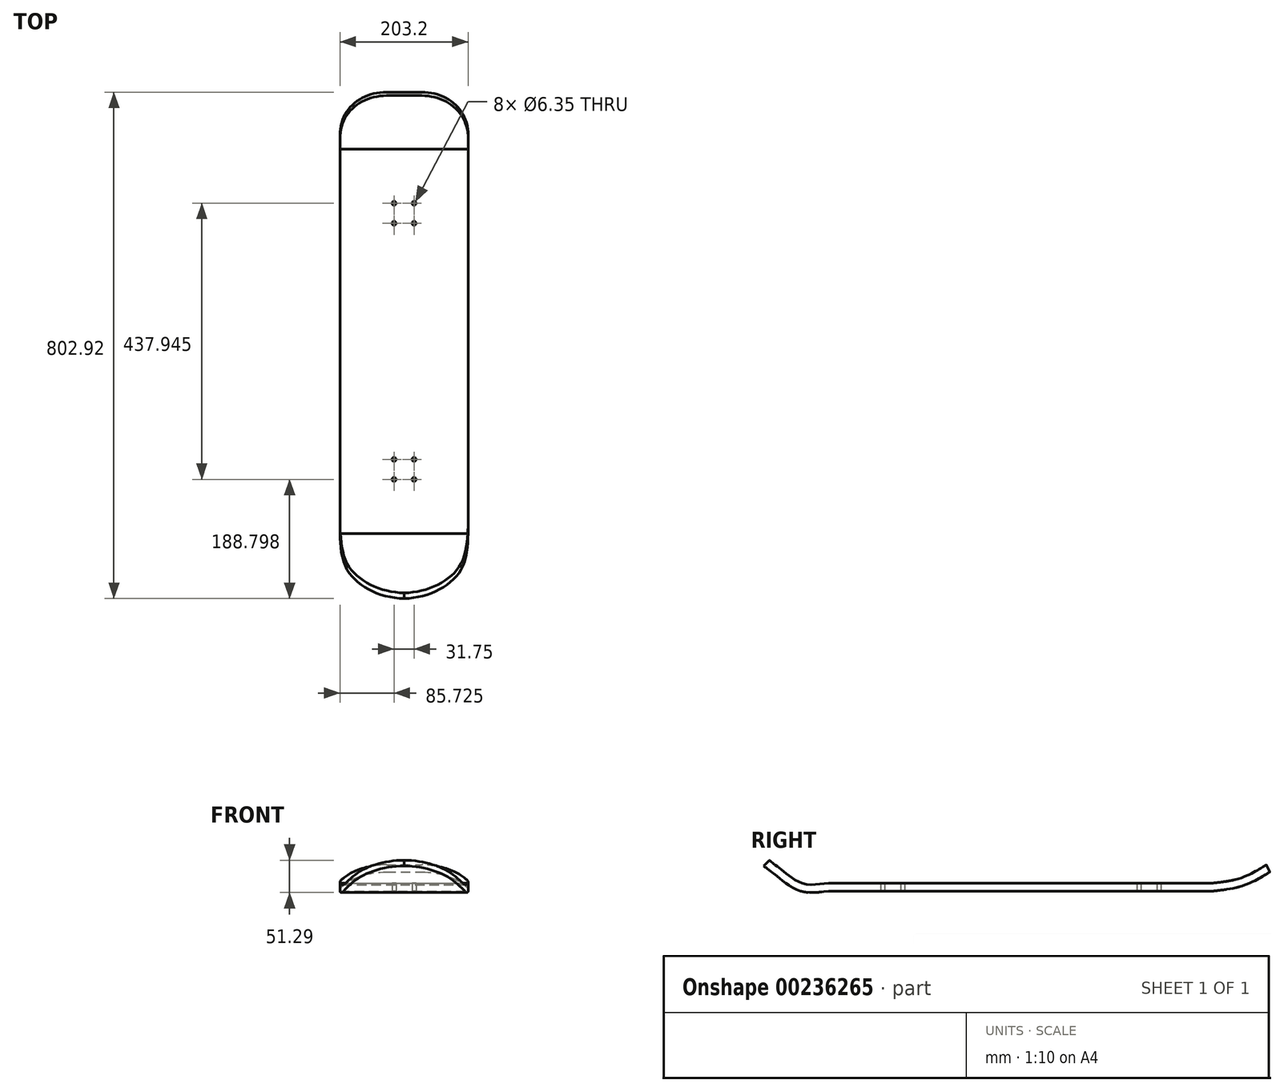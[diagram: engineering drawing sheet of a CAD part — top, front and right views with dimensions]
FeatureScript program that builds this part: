
annotation { "Feature Type Name" : "Feature", "Feature Type Description" : "" }
export const myFeature = defineFeature(function(context is Context, id is Id, definition is map)
    precondition{}
    {
        {
            var Q0;
            Q0=qCreatedBy(makeId("Top.planeOp"),FACE);
            var sketch = newSketch(context, id + "F0", { "sketchPlane" : qUnion([Q0])});
            skLineSegment(sketch, "E0.bottom", {"start": v(-101.6, 304.8) * mm, "end": v(101.6, 304.8) * mm});
            skLineSegment(sketch, "E0.top", {"start": v(-101.6, -304.8) * mm, "end": v(101.6, -304.8) * mm});
            skLineSegment(sketch, "E0.left", {"start": v(-101.6, 304.8) * mm, "end": v(-101.6, -304.8) * mm});
            skLineSegment(sketch, "E0.right", {"start": v(101.6, 304.8) * mm, "end": v(101.6, -304.8) * mm});
            skPoint(sketch, "E0.middle", {"position": v(0, 0) * mm});
            skPoint(sketch, "E1.middle", {"position": v(0, 203.1) * mm});
            skCircle(sketch, "E2", {"center": v(-15.88, 218.97) * mm, "radius": 3.18 * mm});
            skCircle(sketch, "E3", {"center": v(15.87, 218.97) * mm, "radius": 3.18 * mm});
            skCircle(sketch, "E4", {"center": v(-15.87, 187.22) * mm, "radius": 3.18 * mm});
            skCircle(sketch, "E5", {"center": v(15.88, 187.22) * mm, "radius": 3.18 * mm});
            skPoint(sketch, "E1.right.start.orphan", {"position": v(25.4, 228.5) * mm});
            skPoint(sketch, "E1.top.end.orphan", {"position": v(25.4, 177.7) * mm});
            skPoint(sketch, "E1.left.end.orphan", {"position": v(-25.4, 177.7) * mm});
            skPoint(sketch, "E1.left.start.orphan", {"position": v(-25.4, 228.5) * mm});
            skCircle(sketch, "E6.MirrorC", {"center": v(15.87, 187.22) * mm, "radius": 3.18 * mm});
            skCircle(sketch, "E7.MirrorC", {"center": v(-15.87, 218.97) * mm, "radius": 3.18 * mm});
            skCircle(sketch, "E8.MirrorC", {"center": v(15.87, -187.22) * mm, "radius": 3.18 * mm});
            skCircle(sketch, "E9.MirrorC", {"center": v(-15.87, -187.22) * mm, "radius": 3.18 * mm});
            skCircle(sketch, "E10.MirrorC", {"center": v(-15.87, -218.97) * mm, "radius": 3.18 * mm});
            skCircle(sketch, "E11.MirrorC", {"center": v(15.87, -218.97) * mm, "radius": 3.18 * mm});
            skSolve(sketch);
        }
        {
            var Q0;
            Q0 = qSketchRegion(id + "F0", true);
            extrude(context, id + "F1", {"entities" : qUnion([Q0]), "endBound" : BoundingType.SYMMETRIC, "depth" : 12.7 * mm});
        }
        {
            var Q0;
            Q0=qCreatedBy(makeId("Right.planeOp"),FACE);
            var sketch = newSketch(context, id + "F2", { "sketchPlane" : qUnion([Q0])});
            skPoint(sketch, "E12.0.internal.orphan", {"position": v(306.44, 0) * mm});
            skFitSpline(sketch, "E13", {"points": [v(306.44, 0) * mm, v(346.85, 6.88) * mm, v(377.34, 20.38) * mm, v(393.83, 30.37) * mm], "startDerivative": vector(107.37, 11.84) * mm, "endDerivative": vector(57.3, 36.33) * mm});
            skFitSpline(sketch, "E14", {"points": [v(-306.8, 0) * mm, v(-347.15, 0) * mm, v(-379.78, 20.25) * mm, v(-404.74, 39.5) * mm], "startDerivative": vector(-119.67, -15.86) * mm, "endDerivative": vector(-78.2, 59.27) * mm});
            skSolve(sketch);
        }
        {
            var Q0;
            Q0=makeQuery(id+"F1.opExtrude","SWEPT_FACE",FACE,{"disambiguationData":[OSD([sQuery(id+"F0.wireOp",EDGE,"E0.bottom")])]});
            var Q1;
            Q1=sQuery(id+"F2.wireOp",EDGE,"E13");
            sweep(context, id + "F3", {"operationType" : NewBodyOperationType.ADD, "profiles" : qUnion([Q0]), "path" : qUnion([Q1])});
        }
        {
            var Q0;
            Q0=makeQuery(id+"F1.opExtrude","SWEPT_FACE",FACE,{"disambiguationData":[OSD([sQuery(id+"F0.wireOp",EDGE,"E0.top")])]});
            var Q1;
            Q1=sQuery(id+"F2.wireOp",EDGE,"E14");
            sweep(context, id + "F4", {"operationType" : NewBodyOperationType.ADD, "profiles" : qUnion([Q0]), "path" : qUnion([Q1])});
        }
        {
            var Q0;
            Q0=makeQuery(id+"F4.opSweep","CAP_EDGE",EDGE,{"disambiguationData":[OSD([sQuery(id+"F0.wireOp",EDGE,"E0.top"),sQuery(id+"F0.wireOp",EDGE,"E0.right"),sQuery(id+"F2.wireOp",VERTEX,"E14.end")])],"isStart":false});
            var Q1;
            Q1=makeQuery(id+"F4.opSweep","CAP_EDGE",EDGE,{"disambiguationData":[OSD([sQuery(id+"F0.wireOp",EDGE,"E0.top"),sQuery(id+"F0.wireOp",EDGE,"E0.left"),sQuery(id+"F2.wireOp",VERTEX,"E14.end")])],"isStart":false});
            fillet(context, id + "F5", {"entities" : qUnion([Q0, Q1]), "radius" : 103.63 * mm, "tangentPropagation" : true, "allowEdgeOverflow" : false});
        }
        {
            var Q0;
            Q0=makeQuery(id+"F3.opSweep","CAP_EDGE",EDGE,{"disambiguationData":[OSD([sQuery(id+"F0.wireOp",EDGE,"E0.bottom"),sQuery(id+"F0.wireOp",EDGE,"E0.right"),sQuery(id+"F2.wireOp",VERTEX,"E13.end")])],"isStart":false});
            var Q1;
            Q1=makeQuery(id+"F3.opSweep","CAP_EDGE",EDGE,{"disambiguationData":[OSD([sQuery(id+"F0.wireOp",EDGE,"E0.bottom"),sQuery(id+"F0.wireOp",EDGE,"E0.left"),sQuery(id+"F2.wireOp",VERTEX,"E13.end")])],"isStart":false});
            fillet(context, id + "F6", {"entities" : qUnion([Q0, Q1]), "radius" : 73.6 * mm, "tangentPropagation" : true, "allowEdgeOverflow" : false});
        }
    });
